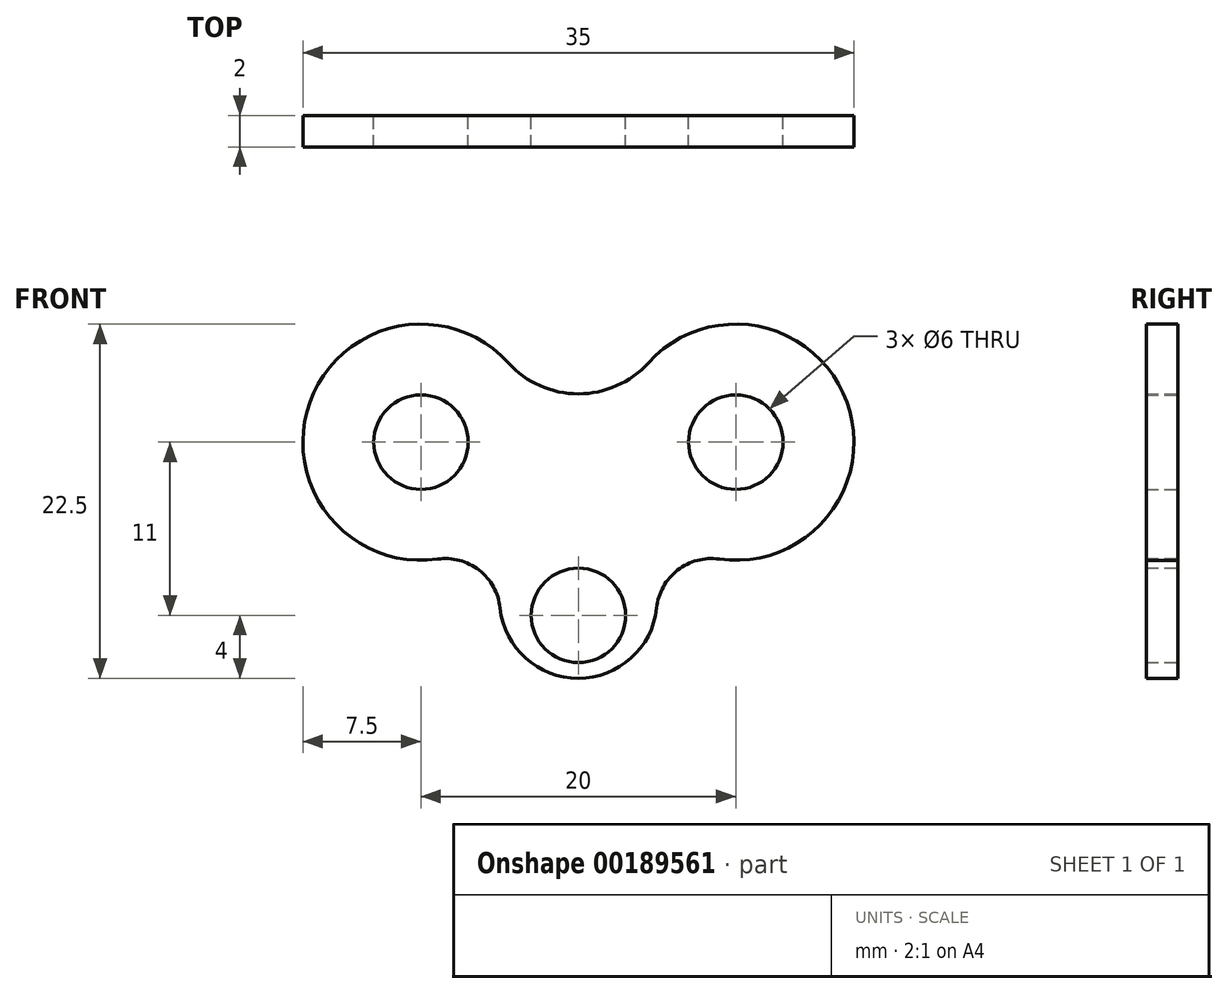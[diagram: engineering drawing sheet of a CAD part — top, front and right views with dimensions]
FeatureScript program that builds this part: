
annotation { "Feature Type Name" : "Feature", "Feature Type Description" : "" }
export const myFeature = defineFeature(function(context is Context, id is Id, definition is map)
    precondition{}
    {
        {
            var Q0;
            Q0=qCreatedBy(makeId("Front.planeOp"),FACE);
            var sketch = newSketch(context, id + "F0", { "sketchPlane" : qUnion([Q0])});
            skLineSegment(sketch, "E0", {"start": v(0, 0) * mm, "end": v(10, 0) * mm, "construction": true});
            skLineSegment(sketch, "E1", {"start": v(0, 0) * mm, "end": v(-10, 0) * mm, "construction": true});
            skLineSegment(sketch, "E2", {"start": v(0, 0) * mm, "end": v(0, -10) * mm, "construction": true});
            skArc(sketch, "E3", {"start": v(-4.44, 5.04) * mm, "mid": v(-17.05, 2.55) * mm, "end": v(-8.95, -7.43) * mm});
            skArc(sketch, "E4", {"start": v(8.95, -7.43) * mm, "mid": v(17.05, 2.55) * mm, "end": v(4.44, 5.04) * mm});
            skArc(sketch, "E5", {"start": v(-4.97, -10.52) * mm, "mid": v(0, -15) * mm, "end": v(4.97, -10.52) * mm});
            skArc(sketch, "E6", {"start": v(-4.44, 5.04) * mm, "mid": v(0, 3.07) * mm, "end": v(4.44, 5.04) * mm});
            skArc(sketch, "E7", {"start": v(8.95, -7.43) * mm, "mid": v(6.3, -8.13) * mm, "end": v(4.97, -10.52) * mm});
            skArc(sketch, "E8", {"start": v(-4.97, -10.52) * mm, "mid": v(-6.3, -8.13) * mm, "end": v(-8.95, -7.43) * mm});
            skCircle(sketch, "E9", {"center": v(10, 0) * mm, "radius": 3 * mm});
            skCircle(sketch, "E10", {"center": v(-10, 0) * mm, "radius": 3 * mm});
            skCircle(sketch, "E11", {"center": v(0, -11) * mm, "radius": 3 * mm});
            skSolve(sketch);
        }
        {
            var Q0;
            Q0=makeQuery(id+"F0.imprint","IMPRINT",FACE,{"disambiguationData":[TD([[makeQuery(id+"F0.imprint","IMPRINT",EDGE,{"derivedFrom":sQuery(id+"F0.wireOp",EDGE,"E3")}),1.0]])]});
            extrude(context, id + "F1", {"entities" : qUnion([Q0]), "depth" : 2 * mm});
        }
    });
